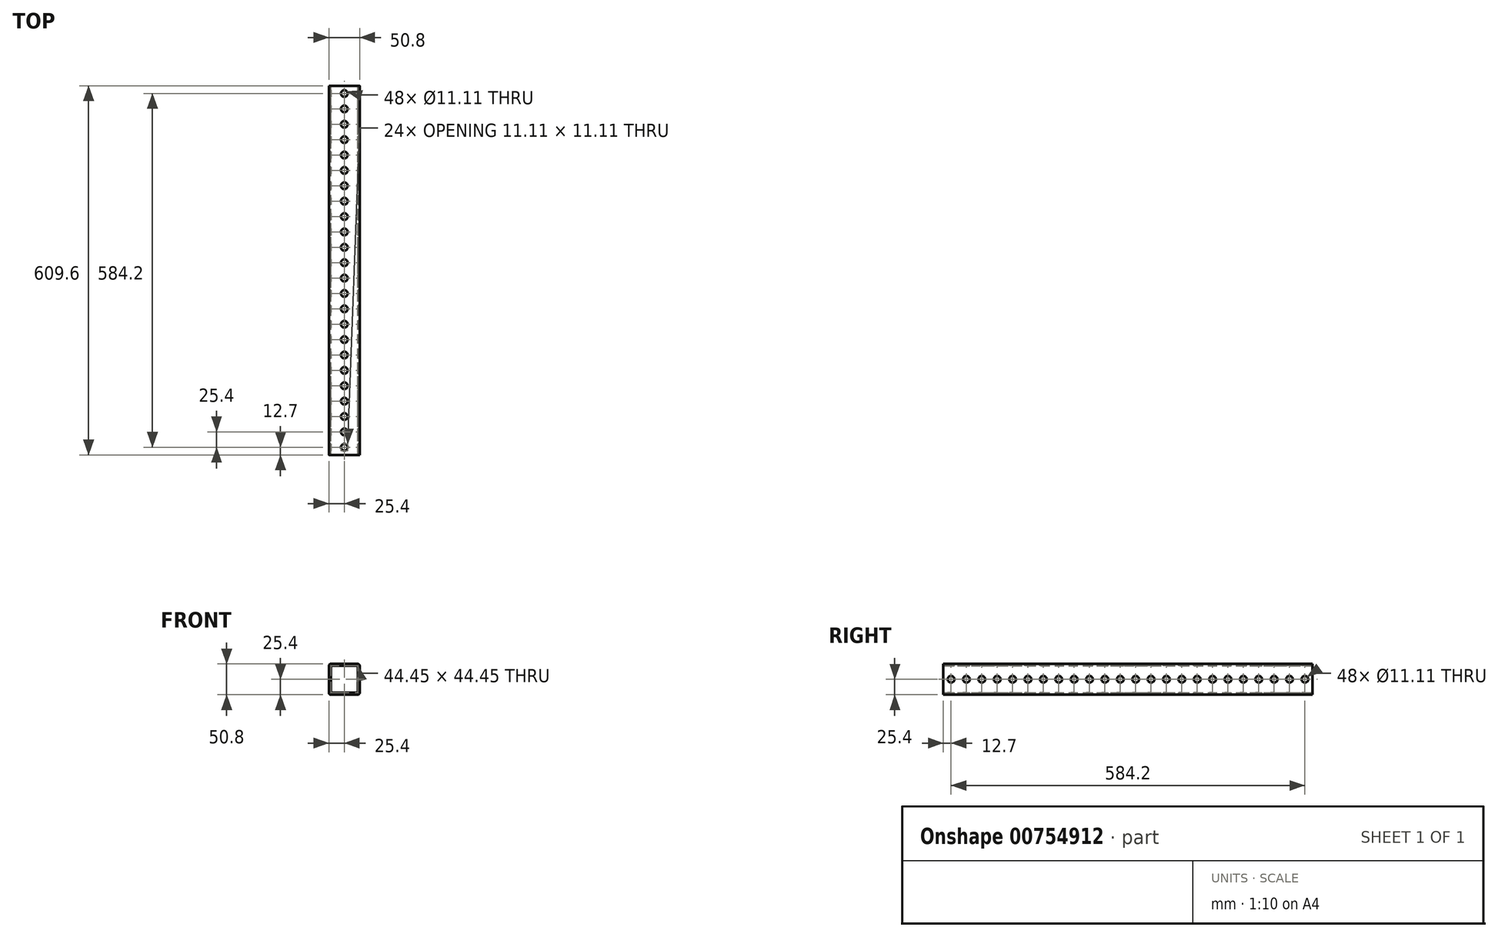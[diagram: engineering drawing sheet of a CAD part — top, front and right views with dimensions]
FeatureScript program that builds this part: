
annotation { "Feature Type Name" : "Feature", "Feature Type Description" : "" }
export const myFeature = defineFeature(function(context is Context, id is Id, definition is map)
    precondition{}
    {
        {
            var Q0;
            Q0=qCreatedBy(makeId("Front.planeOp"),FACE);
            var sketch = newSketch(context, id + "F0", { "sketchPlane" : qUnion([Q0])});
            skLineSegment(sketch, "E0.bottom", {"start": v(-3.18, 0) * mm, "end": v(-47.63, 0) * mm});
            skLineSegment(sketch, "E0.top", {"start": v(-3.17, 50.8) * mm, "end": v(-47.63, 50.8) * mm});
            skLineSegment(sketch, "E0.left", {"start": v(0, 3.18) * mm, "end": v(0, 47.63) * mm});
            skLineSegment(sketch, "E0.right", {"start": v(-50.8, 3.17) * mm, "end": v(-50.8, 47.62) * mm});
            skPoint(sketch, "E1.visualSharp", {"position": v(-50.8, 50.8) * mm});
            skArc(sketch, "E1.filletArc", {"start": v(-47.63, 50.8) * mm, "mid": v(-49.87, 49.87) * mm, "end": v(-50.8, 47.62) * mm});
            skPoint(sketch, "E2.visualSharp", {"position": v(0, 50.8) * mm});
            skArc(sketch, "E2.filletArc", {"start": v(0, 47.63) * mm, "mid": v(-0.93, 49.87) * mm, "end": v(-3.17, 50.8) * mm});
            skPoint(sketch, "E3.visualSharp", {"position": v(0, 0) * mm});
            skArc(sketch, "E3.filletArc", {"start": v(-3.18, 0) * mm, "mid": v(-0.93, 0.93) * mm, "end": v(0, 3.18) * mm});
            skPoint(sketch, "E4.visualSharp", {"position": v(-50.8, 0) * mm});
            skArc(sketch, "E4.filletArc", {"start": v(-50.8, 3.17) * mm, "mid": v(-49.87, 0.93) * mm, "end": v(-47.63, 0) * mm});
            skLineSegment(sketch, "E5.0", {"start": v(-3.18, 3.18) * mm, "end": v(-47.62, 3.17) * mm});
            skLineSegment(sketch, "E5.1", {"start": v(-3.18, 3.18) * mm, "end": v(-3.18, 47.63) * mm});
            skLineSegment(sketch, "E5.2", {"start": v(-3.18, 47.63) * mm, "end": v(-47.63, 47.62) * mm});
            skLineSegment(sketch, "E5.3", {"start": v(-47.62, 3.17) * mm, "end": v(-47.63, 47.62) * mm});
            skSolve(sketch);
        }
        {
            var Q0;
            Q0=makeQuery(id+"F0.imprint","IMPRINT",FACE,{"disambiguationData":[TD([[makeQuery(id+"F0.imprint","IMPRINT",EDGE,{"derivedFrom":sQuery(id+"F0.wireOp",EDGE,"E0.bottom")}),-1.0]])]});
            extrude(context, id + "F1", {"entities" : qUnion([Q0]), "endBound" : BoundingType.SYMMETRIC, "depth" : 609.6 * mm, "offsetDistance" : 25.4 * mm});
        }
        {
            var Q0;
            Q0=makeQuery(id+"F1.opExtrude","SWEPT_FACE",FACE,{"disambiguationData":[OSD([sQuery(id+"F0.wireOp",EDGE,"E0.right")])]});
            var sketch = newSketch(context, id + "F2", { "sketchPlane" : qUnion([Q0])});
            skLineSegment(sketch, "E6", {"start": v(-292.1, 3.17) * mm, "end": v(-292.1, 47.63) * mm, "construction": true});
            skLineSegment(sketch, "E7", {"start": v(-304.8, 25.4) * mm, "end": v(-292.1, 25.4) * mm, "construction": true});
            skCircle(sketch, "E8", {"center": v(-292.1, 25.4) * mm, "radius": 5.56 * mm});
            skCircle(sketch, "E9.1.0.0", {"center": v(-266.7, 25.4) * mm, "radius": 5.56 * mm});
            skCircle(sketch, "E9.2.0.0", {"center": v(-241.3, 25.4) * mm, "radius": 5.56 * mm});
            skCircle(sketch, "E9.3.0.0", {"center": v(-215.9, 25.4) * mm, "radius": 5.56 * mm});
            skCircle(sketch, "E9.4.0.0", {"center": v(-190.5, 25.4) * mm, "radius": 5.56 * mm});
            skCircle(sketch, "E9.5.0.0", {"center": v(-165.1, 25.4) * mm, "radius": 5.56 * mm});
            skCircle(sketch, "E9.6.0.0", {"center": v(-139.7, 25.4) * mm, "radius": 5.56 * mm});
            skCircle(sketch, "E9.7.0.0", {"center": v(-114.3, 25.4) * mm, "radius": 5.56 * mm});
            skCircle(sketch, "E9.8.0.0", {"center": v(-88.9, 25.4) * mm, "radius": 5.56 * mm});
            skCircle(sketch, "E9.9.0.0", {"center": v(-63.5, 25.4) * mm, "radius": 5.56 * mm});
            skCircle(sketch, "E9.10.0.0", {"center": v(-38.1, 25.4) * mm, "radius": 5.56 * mm});
            skCircle(sketch, "E9.11.0.0", {"center": v(-12.7, 25.4) * mm, "radius": 5.56 * mm});
            skCircle(sketch, "E9.12.0.0", {"center": v(12.7, 25.4) * mm, "radius": 5.56 * mm});
            skCircle(sketch, "E9.13.0.0", {"center": v(38.1, 25.4) * mm, "radius": 5.56 * mm});
            skCircle(sketch, "E9.14.0.0", {"center": v(63.5, 25.4) * mm, "radius": 5.56 * mm});
            skCircle(sketch, "E9.15.0.0", {"center": v(88.9, 25.4) * mm, "radius": 5.56 * mm});
            skCircle(sketch, "E9.16.0.0", {"center": v(114.3, 25.4) * mm, "radius": 5.56 * mm});
            skCircle(sketch, "E9.17.0.0", {"center": v(139.7, 25.4) * mm, "radius": 5.56 * mm});
            skCircle(sketch, "E9.18.0.0", {"center": v(165.1, 25.4) * mm, "radius": 5.56 * mm});
            skCircle(sketch, "E9.19.0.0", {"center": v(190.5, 25.4) * mm, "radius": 5.56 * mm});
            skCircle(sketch, "E9.20.0.0", {"center": v(215.9, 25.4) * mm, "radius": 5.56 * mm});
            skCircle(sketch, "E9.21.0.0", {"center": v(241.3, 25.4) * mm, "radius": 5.56 * mm});
            skCircle(sketch, "E9.22.0.0", {"center": v(266.7, 25.4) * mm, "radius": 5.56 * mm});
            skCircle(sketch, "E9.23.0.0", {"center": v(292.1, 25.4) * mm, "radius": 5.56 * mm});
            skLineSegment(sketch, "E9.direction1", {"start": v(-292.1, 25.4) * mm, "end": v(-266.7, 25.4) * mm, "construction": true});
            skSolve(sketch);
        }
        {
            var Q0;
            Q0=qSketchRegion(id+"F2",true);
            extrude(context, id + "F3", {"entities" : qUnion([Q0]), "operationType" : NewBodyOperationType.REMOVE, "oppositeDirection" : true, "depth" : 50.8 * mm, "offsetDistance" : 25.4 * mm});
        }
        {
            var Q0;
            Q0=makeQuery(id+"F1.opExtrude","SWEPT_FACE",FACE,{"disambiguationData":[OSD([sQuery(id+"F0.wireOp",EDGE,"E0.top")])]});
            var sketch = newSketch(context, id + "F4", { "sketchPlane" : qUnion([Q0])});
            skCircle(sketch, "E10", {"center": v(-25.4, 292.1) * mm, "radius": 5.56 * mm});
            skPoint(sketch, "E10.centerSnap0", {"position": v(-25.4, 304.8) * mm});
            skCircle(sketch, "E11.0.1.0", {"center": v(-25.4, 266.7) * mm, "radius": 5.56 * mm});
            skCircle(sketch, "E11.0.2.0", {"center": v(-25.4, 241.3) * mm, "radius": 5.56 * mm});
            skCircle(sketch, "E11.0.3.0", {"center": v(-25.4, 215.9) * mm, "radius": 5.56 * mm});
            skCircle(sketch, "E11.0.4.0", {"center": v(-25.4, 190.5) * mm, "radius": 5.56 * mm});
            skCircle(sketch, "E11.0.5.0", {"center": v(-25.4, 165.1) * mm, "radius": 5.56 * mm});
            skCircle(sketch, "E11.0.6.0", {"center": v(-25.4, 139.7) * mm, "radius": 5.56 * mm});
            skCircle(sketch, "E11.0.7.0", {"center": v(-25.4, 114.3) * mm, "radius": 5.56 * mm});
            skCircle(sketch, "E11.0.8.0", {"center": v(-25.4, 88.9) * mm, "radius": 5.56 * mm});
            skCircle(sketch, "E11.0.9.0", {"center": v(-25.4, 63.5) * mm, "radius": 5.56 * mm});
            skCircle(sketch, "E11.0.10.0", {"center": v(-25.4, 38.1) * mm, "radius": 5.56 * mm});
            skCircle(sketch, "E11.0.11.0", {"center": v(-25.4, 12.7) * mm, "radius": 5.56 * mm});
            skCircle(sketch, "E11.0.12.0", {"center": v(-25.4, -12.7) * mm, "radius": 5.56 * mm});
            skCircle(sketch, "E11.0.13.0", {"center": v(-25.4, -38.1) * mm, "radius": 5.56 * mm});
            skCircle(sketch, "E11.0.14.0", {"center": v(-25.4, -63.5) * mm, "radius": 5.56 * mm});
            skCircle(sketch, "E11.0.15.0", {"center": v(-25.4, -88.9) * mm, "radius": 5.56 * mm});
            skCircle(sketch, "E11.0.16.0", {"center": v(-25.4, -114.3) * mm, "radius": 5.56 * mm});
            skCircle(sketch, "E11.0.17.0", {"center": v(-25.4, -139.7) * mm, "radius": 5.56 * mm});
            skCircle(sketch, "E11.0.18.0", {"center": v(-25.4, -165.1) * mm, "radius": 5.56 * mm});
            skCircle(sketch, "E11.0.19.0", {"center": v(-25.4, -190.5) * mm, "radius": 5.56 * mm});
            skCircle(sketch, "E11.0.20.0", {"center": v(-25.4, -215.9) * mm, "radius": 5.56 * mm});
            skCircle(sketch, "E11.0.21.0", {"center": v(-25.4, -241.3) * mm, "radius": 5.56 * mm});
            skCircle(sketch, "E11.0.22.0", {"center": v(-25.4, -266.7) * mm, "radius": 5.56 * mm});
            skCircle(sketch, "E11.0.23.0", {"center": v(-25.4, -292.1) * mm, "radius": 5.56 * mm});
            skLineSegment(sketch, "E11.direction1", {"start": v(-25.4, 292.1) * mm, "end": v(0, 292.1) * mm, "construction": true});
            skLineSegment(sketch, "E11.direction2", {"start": v(-25.4, 292.1) * mm, "end": v(-25.4, 266.7) * mm, "construction": true});
            skSolve(sketch);
        }
        {
            var Q0;
            Q0=makeQuery(id+"F4.imprint","IMPRINT",FACE,{"disambiguationData":[TD([[makeQuery(id+"F4.imprint","IMPRINT",EDGE,{"derivedFrom":sQuery(id+"F4.wireOp",EDGE,"E11.0.23.0")}),1.0]])]});
            var Q1;
            Q1=makeQuery(id+"F4.imprint","IMPRINT",FACE,{"disambiguationData":[TD([[makeQuery(id+"F4.imprint","IMPRINT",EDGE,{"derivedFrom":sQuery(id+"F4.wireOp",EDGE,"E11.0.22.0")}),1.0]])]});
            var Q2;
            Q2=makeQuery(id+"F4.imprint","IMPRINT",FACE,{"disambiguationData":[TD([[makeQuery(id+"F4.imprint","IMPRINT",EDGE,{"derivedFrom":sQuery(id+"F4.wireOp",EDGE,"E11.0.21.0")}),1.0]])]});
            var Q3;
            Q3=makeQuery(id+"F4.imprint","IMPRINT",FACE,{"disambiguationData":[TD([[makeQuery(id+"F4.imprint","IMPRINT",EDGE,{"derivedFrom":sQuery(id+"F4.wireOp",EDGE,"E11.0.20.0")}),1.0]])]});
            var Q4;
            Q4=makeQuery(id+"F4.imprint","IMPRINT",FACE,{"disambiguationData":[TD([[makeQuery(id+"F4.imprint","IMPRINT",EDGE,{"derivedFrom":sQuery(id+"F4.wireOp",EDGE,"E11.0.19.0")}),1.0]])]});
            var Q5;
            Q5=makeQuery(id+"F4.imprint","IMPRINT",FACE,{"disambiguationData":[TD([[makeQuery(id+"F4.imprint","IMPRINT",EDGE,{"derivedFrom":sQuery(id+"F4.wireOp",EDGE,"E11.0.18.0")}),1.0]])]});
            var Q6;
            Q6=makeQuery(id+"F4.imprint","IMPRINT",FACE,{"disambiguationData":[TD([[makeQuery(id+"F4.imprint","IMPRINT",EDGE,{"derivedFrom":sQuery(id+"F4.wireOp",EDGE,"E11.0.17.0")}),1.0]])]});
            var Q7;
            Q7=makeQuery(id+"F4.imprint","IMPRINT",FACE,{"disambiguationData":[TD([[makeQuery(id+"F4.imprint","IMPRINT",EDGE,{"derivedFrom":sQuery(id+"F4.wireOp",EDGE,"E11.0.16.0")}),1.0]])]});
            var Q8;
            Q8=makeQuery(id+"F4.imprint","IMPRINT",FACE,{"disambiguationData":[TD([[makeQuery(id+"F4.imprint","IMPRINT",EDGE,{"derivedFrom":sQuery(id+"F4.wireOp",EDGE,"E11.0.15.0")}),1.0]])]});
            var Q9;
            Q9=makeQuery(id+"F4.imprint","IMPRINT",FACE,{"disambiguationData":[TD([[makeQuery(id+"F4.imprint","IMPRINT",EDGE,{"derivedFrom":sQuery(id+"F4.wireOp",EDGE,"E11.0.14.0")}),1.0]])]});
            var Q10;
            Q10=makeQuery(id+"F4.imprint","IMPRINT",FACE,{"disambiguationData":[TD([[makeQuery(id+"F4.imprint","IMPRINT",EDGE,{"derivedFrom":sQuery(id+"F4.wireOp",EDGE,"E11.0.13.0")}),1.0]])]});
            var Q11;
            Q11=makeQuery(id+"F4.imprint","IMPRINT",FACE,{"disambiguationData":[TD([[makeQuery(id+"F4.imprint","IMPRINT",EDGE,{"derivedFrom":sQuery(id+"F4.wireOp",EDGE,"E11.0.12.0")}),1.0]])]});
            var Q12;
            Q12=makeQuery(id+"F4.imprint","IMPRINT",FACE,{"disambiguationData":[TD([[makeQuery(id+"F4.imprint","IMPRINT",EDGE,{"derivedFrom":sQuery(id+"F4.wireOp",EDGE,"E11.0.11.0")}),1.0]])]});
            var Q13;
            Q13=makeQuery(id+"F4.imprint","IMPRINT",FACE,{"disambiguationData":[TD([[makeQuery(id+"F4.imprint","IMPRINT",EDGE,{"derivedFrom":sQuery(id+"F4.wireOp",EDGE,"E11.0.10.0")}),1.0]])]});
            var Q14;
            Q14=makeQuery(id+"F4.imprint","IMPRINT",FACE,{"disambiguationData":[TD([[makeQuery(id+"F4.imprint","IMPRINT",EDGE,{"derivedFrom":sQuery(id+"F4.wireOp",EDGE,"E11.0.9.0")}),1.0]])]});
            var Q15;
            Q15=makeQuery(id+"F4.imprint","IMPRINT",FACE,{"disambiguationData":[TD([[makeQuery(id+"F4.imprint","IMPRINT",EDGE,{"derivedFrom":sQuery(id+"F4.wireOp",EDGE,"E11.0.8.0")}),1.0]])]});
            var Q16;
            Q16=makeQuery(id+"F4.imprint","IMPRINT",FACE,{"disambiguationData":[TD([[makeQuery(id+"F4.imprint","IMPRINT",EDGE,{"derivedFrom":sQuery(id+"F4.wireOp",EDGE,"E11.0.7.0")}),1.0]])]});
            var Q17;
            Q17=makeQuery(id+"F4.imprint","IMPRINT",FACE,{"disambiguationData":[TD([[makeQuery(id+"F4.imprint","IMPRINT",EDGE,{"derivedFrom":sQuery(id+"F4.wireOp",EDGE,"E11.0.6.0")}),1.0]])]});
            var Q18;
            Q18=makeQuery(id+"F4.imprint","IMPRINT",FACE,{"disambiguationData":[TD([[makeQuery(id+"F4.imprint","IMPRINT",EDGE,{"derivedFrom":sQuery(id+"F4.wireOp",EDGE,"E11.0.5.0")}),1.0]])]});
            var Q19;
            Q19=makeQuery(id+"F4.imprint","IMPRINT",FACE,{"disambiguationData":[TD([[makeQuery(id+"F4.imprint","IMPRINT",EDGE,{"derivedFrom":sQuery(id+"F4.wireOp",EDGE,"E11.0.4.0")}),1.0]])]});
            var Q20;
            Q20=makeQuery(id+"F4.imprint","IMPRINT",FACE,{"disambiguationData":[TD([[makeQuery(id+"F4.imprint","IMPRINT",EDGE,{"derivedFrom":sQuery(id+"F4.wireOp",EDGE,"E11.0.3.0")}),1.0]])]});
            var Q21;
            Q21=makeQuery(id+"F4.imprint","IMPRINT",FACE,{"disambiguationData":[TD([[makeQuery(id+"F4.imprint","IMPRINT",EDGE,{"derivedFrom":sQuery(id+"F4.wireOp",EDGE,"E11.0.2.0")}),1.0]])]});
            var Q22;
            Q22=makeQuery(id+"F4.imprint","IMPRINT",FACE,{"disambiguationData":[TD([[makeQuery(id+"F4.imprint","IMPRINT",EDGE,{"derivedFrom":sQuery(id+"F4.wireOp",EDGE,"E11.0.1.0")}),1.0]])]});
            var Q23;
            Q23=makeQuery(id+"F4.imprint","IMPRINT",FACE,{"disambiguationData":[TD([[makeQuery(id+"F4.imprint","IMPRINT",EDGE,{"derivedFrom":sQuery(id+"F4.wireOp",EDGE,"E10")}),1.0]])]});
            extrude(context, id + "F5", {"entities" : qUnion([Q0, Q1, Q2, Q3, Q4, Q5, Q6, Q7, Q8, Q9, Q10, Q11, Q12, Q13, Q14, Q15, Q16, Q17, Q18, Q19, Q20, Q21, Q22, Q23]), "operationType" : NewBodyOperationType.REMOVE, "oppositeDirection" : true, "depth" : 50.8 * mm, "offsetDistance" : 25.4 * mm});
        }
    });
